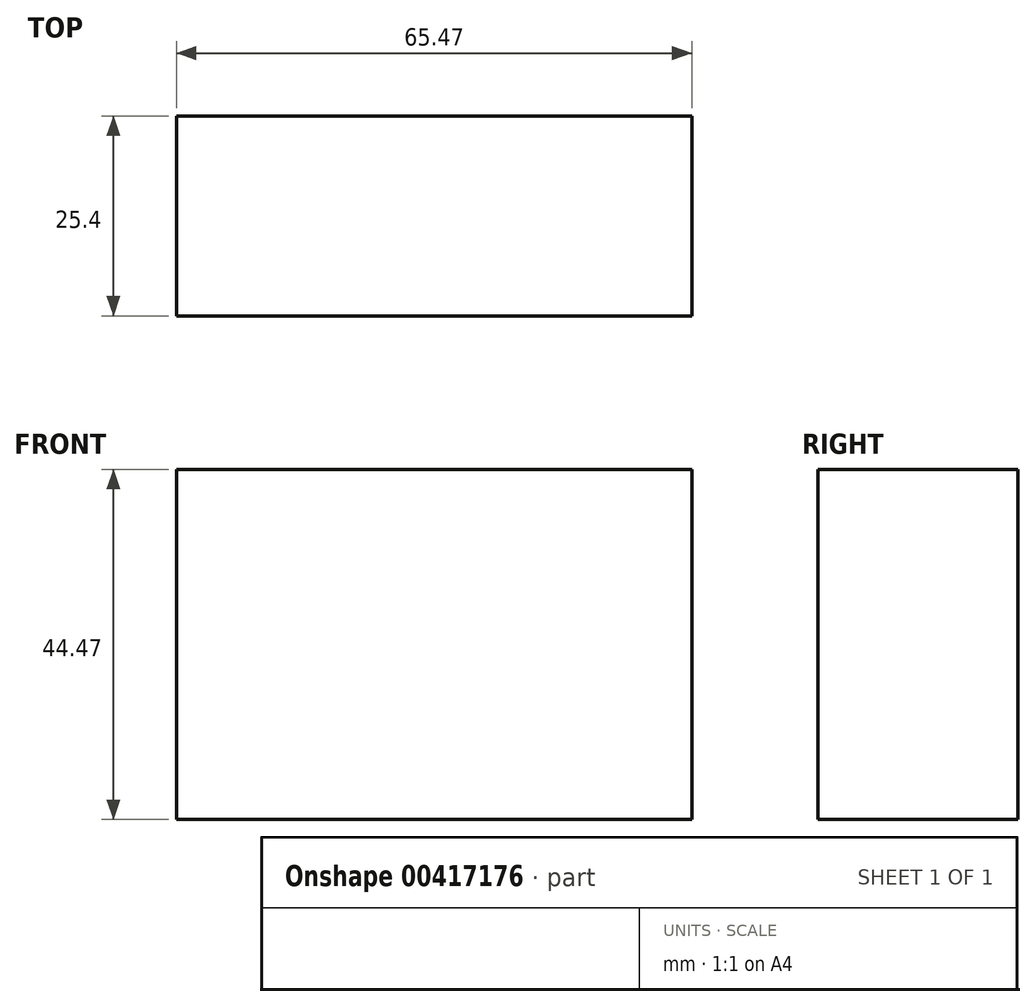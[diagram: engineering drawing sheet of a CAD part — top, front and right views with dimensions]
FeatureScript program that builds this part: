
annotation { "Feature Type Name" : "Feature", "Feature Type Description" : "" }
export const myFeature = defineFeature(function(context is Context, id is Id, definition is map)
    precondition{}
    {
        {
            var Q0;
            Q0=qCreatedBy(makeId("Front.planeOp"),FACE);
            var sketch = newSketch(context, id + "F0", { "sketchPlane" : qUnion([Q0])});
            skLineSegment(sketch, "E0.bottom", {"start": v(0, 0) * mm, "end": v(65.47, 0) * mm});
            skLineSegment(sketch, "E0.top", {"start": v(0, 44.47) * mm, "end": v(65.47, 44.47) * mm});
            skLineSegment(sketch, "E0.left", {"start": v(0, 0) * mm, "end": v(0, 44.47) * mm});
            skLineSegment(sketch, "E0.right", {"start": v(65.47, 0) * mm, "end": v(65.47, 44.47) * mm});
            skSolve(sketch);
        }
        {
            var Q0;
            Q0=makeQuery(id+"F0.imprint","IMPRINT",FACE,{"disambiguationData":[TD([[makeQuery(id+"F0.imprint","IMPRINT",EDGE,{"derivedFrom":sQuery(id+"F0.wireOp",EDGE,"E0.bottom")}),1.0]])]});
            extrude(context, id + "F1", {"entities" : qUnion([Q0]), "depth" : 25.4 * mm});
        }
    });
